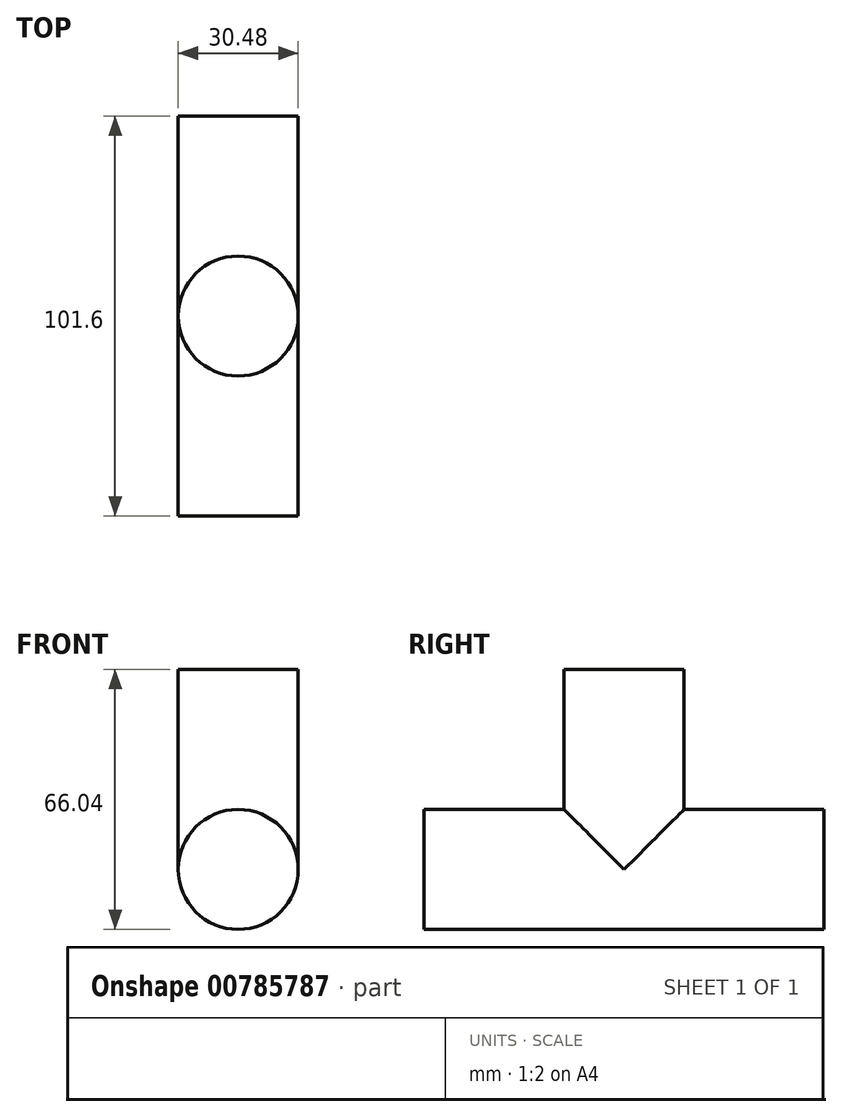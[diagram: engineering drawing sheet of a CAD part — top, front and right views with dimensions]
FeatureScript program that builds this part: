
annotation { "Feature Type Name" : "Feature", "Feature Type Description" : "" }
export const myFeature = defineFeature(function(context is Context, id is Id, definition is map)
    precondition{}
    {
        {
            var Q0;
            Q0=qCreatedBy(makeId("Right.planeOp"),FACE);
            var sketch = newSketch(context, id + "F0", { "sketchPlane" : qUnion([Q0])});
            skLineSegment(sketch, "E0", {"start": v(0, 0) * mm, "end": v(50.8, 0) * mm});
            skLineSegment(sketch, "E1", {"start": v(0, 0) * mm, "end": v(-50.8, 0) * mm});
            skLineSegment(sketch, "E2", {"start": v(0, 0) * mm, "end": v(0, 50.8) * mm});
            skSolve(sketch);
        }
        {
            var Q0;
            Q0=qCreatedBy(makeId("Front.planeOp"),FACE);
            var sketch = newSketch(context, id + "F1", { "sketchPlane" : qUnion([Q0])});
            skCircle(sketch, "E3", {"center": v(0, 0) * mm, "radius": 15.24 * mm});
            skSolve(sketch);
        }
        {
            var Q0;
            Q0=makeQuery(id+"F1.imprint","IMPRINT",FACE,{"disambiguationData":[TD([[makeQuery(id+"F1.imprint","IMPRINT",EDGE,{"derivedFrom":sQuery(id+"F1.wireOp",EDGE,"E3")}),1.0]])]});
            var Q1;
            Q1=sQuery(id+"F0.wireOp",EDGE,"E1");
            var Q2;
            Q2=sQuery(id+"F0.wireOp",EDGE,"E0");
            sweep(context, id + "F2", {"profiles" : qUnion([Q0]), "path" : qUnion([Q1, Q2])});
        }
        {
            var Q0;
            Q0=qCreatedBy(makeId("Top.planeOp"),FACE);
            var sketch = newSketch(context, id + "F3", { "sketchPlane" : qUnion([Q0])});
            skCircle(sketch, "E4", {"center": v(0, 0) * mm, "radius": 15.24 * mm});
            skSolve(sketch);
        }
        {
            var Q0;
            Q0 = qSketchRegion(id + "F3", true);
            var Q1;
            Q1=sQuery(id+"F0.wireOp",EDGE,"E2");
            sweep(context, id + "F4", {"operationType" : NewBodyOperationType.ADD, "profiles" : qUnion([Q0]), "path" : qUnion([Q1])});
        }
    });
